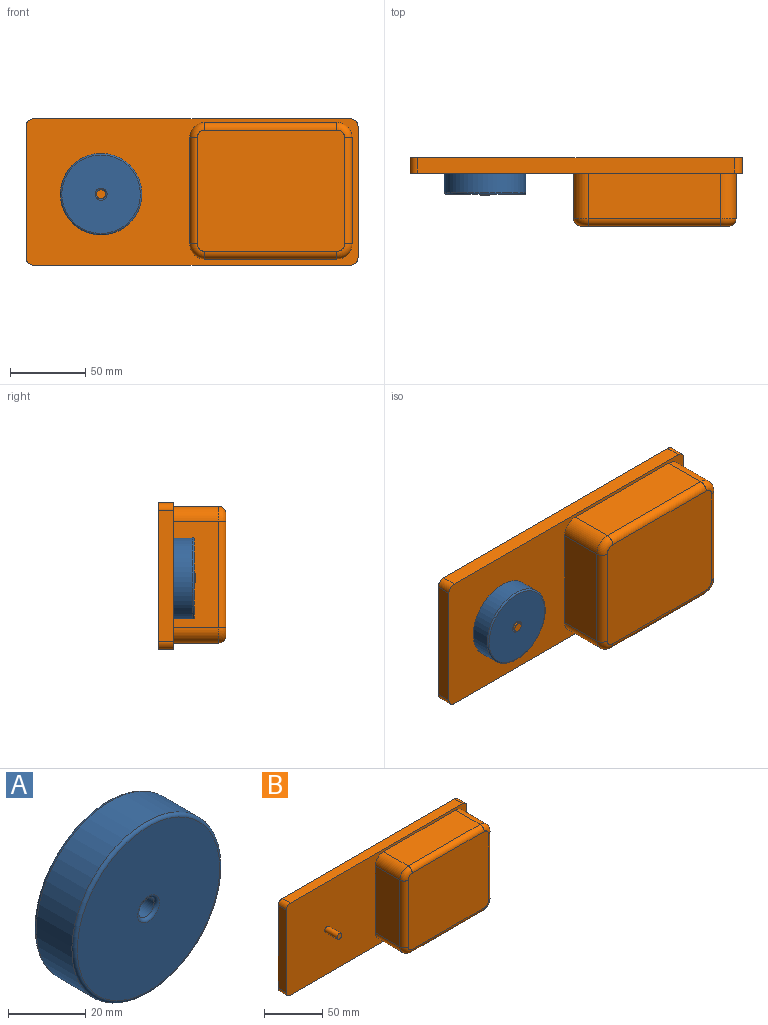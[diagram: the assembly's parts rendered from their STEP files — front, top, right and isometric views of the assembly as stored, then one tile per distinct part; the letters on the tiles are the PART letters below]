
ASSEMBLY  parts=2 mates=1
PART A: 8 faces, bbox 58.4x15x58.4 mm
  f0: cylinder r=3mm len=13mm, axis (0,1,0), area 245mm2, adj f6,f7
  f1: cylinder r=27mm len=54mm, axis (0,1,0), area 2205.4mm2, adj f4,f5
  f2: plane 52x52mm, normal (0,-1,0), area 2073.5mm2, adj f5,f7
  f3: plane 52x52mm, normal (0,1,0), area 2073.5mm2, adj f4,f6
  f4: torus R=26mm, axis (0,-1,0), area 262.9mm2, adj f1,f3
  f5: torus R=26mm, axis (0,-1,0), area 262.9mm2, adj f1,f2
  f6: torus R=4mm, axis (0,-1,0), area 33.2mm2, adj f0,f3
  f7: torus R=4mm, axis (0,-1,0), area 33.2mm2, adj f0,f2
PART B: 29 faces, bbox 220x45x97 mm
  f0: plane 220x97mm, normal (0,-1,0), area 11641.3mm2, adj f1,f2,f3,f4,f6,f7,f8,f9
  f1: plane 210x10mm, normal (0,0,1), area 2100mm2, adj f0,f5,f23,f26
  f2: plane 87x10mm, normal (-1,0,0), area 870mm2, adj f0,f5,f23,f24
  f3: plane 210x10mm, normal (0,0,-1), area 2100mm2, adj f0,f5,f24,f25
  f4: plane 87x10mm, normal (1,0,0), area 870mm2, adj f0,f5,f25,f26
  f5: plane 220x97mm, normal (0,1,0), area 21318.5mm2, adj f1,f2,f3,f4,f23,f24,f25,f26
  f6: plane 87.61x30mm, normal (0,0,1), area 2628.3mm2, adj f0,f12,f14,f22
  f7: plane 70.47x30mm, normal (-1,0,0), area 2113.9mm2, adj f0,f11,f14,f18
  f8: plane 87.61x30mm, normal (0,0,-1), area 2628.3mm2, adj f0,f11,f13,f15
  f9: plane 70.47x30mm, normal (1,0,0), area 2113.9mm2, adj f0,f12,f13,f19
  f10: plane 97.61x80.47mm, normal (0,-1,0), area 7832.6mm2, adj f15,f16,f17,f18,f19,f20,f21,f22
  f11: cylinder r=10mm len=30mm, axis (0,1,0), area 471.2mm2, adj f0,f7,f8,f16
  f12: cylinder r=10mm len=30mm, axis (0,1,0), area 471.2mm2, adj f0,f6,f9,f21
  f13: cylinder r=10mm len=30mm, axis (0,-1,0), area 471.2mm2, adj f0,f8,f9,f17
  f14: cylinder r=10mm len=30mm, axis (0,-1,0), area 471.2mm2, adj f0,f6,f7,f20
  f15: cylinder r=5mm len=87.61mm, axis (-1,0,0), area 688.1mm2, adj f8,f10,f16,f17
  f16: torus R=5mm, axis (0,-1,0), area 101mm2, adj f10,f11,f15,f18
  f17: torus R=5mm, axis (0,-1,0), area 101mm2, adj f10,f13,f15,f19
  f18: cylinder r=5mm len=70.47mm, axis (0,0,1), area 553.4mm2, adj f7,f10,f16,f20
  f19: cylinder r=5mm len=70.47mm, axis (0,0,-1), area 553.4mm2, adj f9,f10,f17,f21
  f20: torus R=5mm, axis (0,-1,0), area 101mm2, adj f10,f14,f18,f22
  f21: torus R=5mm, axis (0,-1,0), area 101mm2, adj f10,f12,f19,f22
  f22: cylinder r=5mm len=87.61mm, axis (1,0,0), area 688.1mm2, adj f6,f10,f20,f21
  f23: cylinder r=5mm len=10mm, axis (0,-1,0), area 78.5mm2, adj f0,f1,f2,f5
  f24: cylinder r=5mm len=10mm, axis (0,1,0), area 78.5mm2, adj f0,f2,f3,f5
  f25: cylinder r=5mm len=10mm, axis (0,-1,0), area 78.5mm2, adj f0,f3,f4,f5
  f26: cylinder r=5mm len=10mm, axis (0,1,0), area 78.5mm2, adj f0,f1,f4,f5
  f27: cylinder r=3mm len=15mm, axis (0,1,0), area 282.7mm2, adj f0,f28
  f28: plane 6x6mm, normal (0,-1,0), area 28.3mm2, adj f27
PLACE A t=(-210.75,-53.01,58.4)mm
PLACE B t=(-68.48,-44.01,3.88)mm
MATE revolute B.f27 <-> A.f0  axis (0,-1,0) through (-210.75,-54.01,58.4)mm
